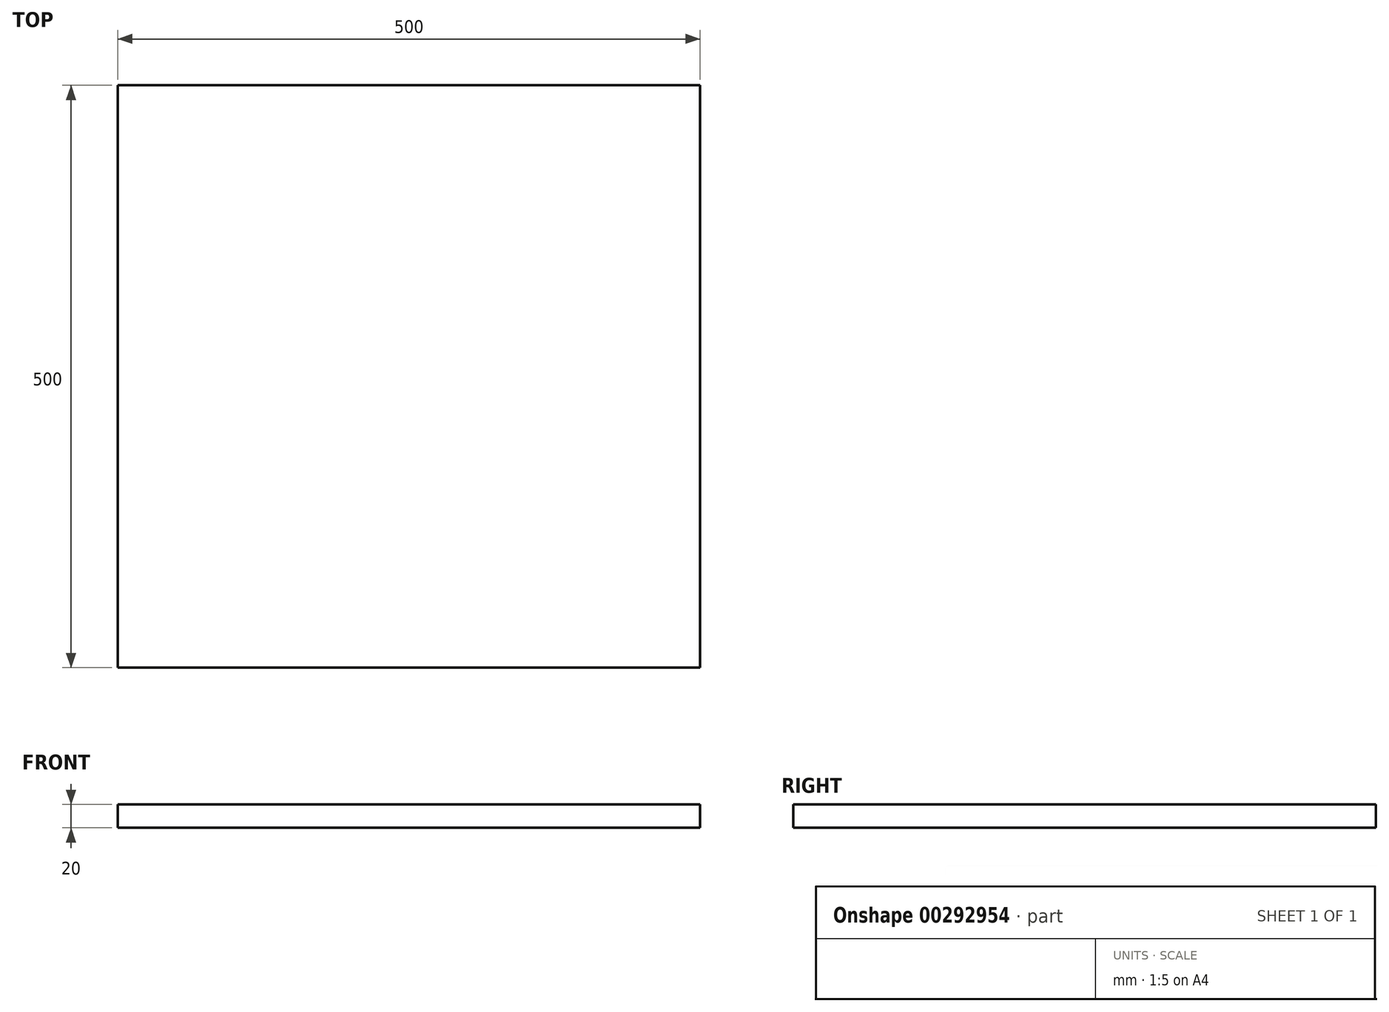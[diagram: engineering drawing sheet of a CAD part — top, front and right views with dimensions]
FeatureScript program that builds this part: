
annotation { "Feature Type Name" : "Feature", "Feature Type Description" : "" }
export const myFeature = defineFeature(function(context is Context, id is Id, definition is map)
    precondition{}
    {
        {
            var Q0;
            Q0=qCreatedBy(makeId("Top.planeOp"),FACE);
            var sketch = newSketch(context, id + "F0", { "sketchPlane" : qUnion([Q0])});
            skLineSegment(sketch, "E0.bottom", {"start": v(250, 250) * mm, "end": v(-250, 250) * mm});
            skLineSegment(sketch, "E0.top", {"start": v(250, -250) * mm, "end": v(-250, -250) * mm});
            skLineSegment(sketch, "E0.left", {"start": v(250, 250) * mm, "end": v(250, -250) * mm});
            skLineSegment(sketch, "E0.right", {"start": v(-250, 250) * mm, "end": v(-250, -250) * mm});
            skPoint(sketch, "E0.middle", {"position": v(0, 0) * mm});
            skSolve(sketch);
        }
        {
            var Q0;
            Q0=makeQuery(id+"F0.imprint","IMPRINT",FACE,{"disambiguationData":[TD([[makeQuery(id+"F0.imprint","IMPRINT",EDGE,{"derivedFrom":sQuery(id+"F0.wireOp",EDGE,"E0.bottom")}),1.0]])]});
            var sketch = newSketch(context, id + "F1", { "sketchPlane" : qUnion([Q0])});
            skLineSegment(sketch, "E1.bottom", {"start": v(-250, 250) * mm, "end": v(250, 250) * mm});
            skLineSegment(sketch, "E1.top", {"start": v(-250, -250) * mm, "end": v(250, -250) * mm});
            skLineSegment(sketch, "E1.left", {"start": v(-250, 250) * mm, "end": v(-250, -250) * mm});
            skLineSegment(sketch, "E1.right", {"start": v(250, 250) * mm, "end": v(250, -250) * mm});
            skPoint(sketch, "E1.middle", {"position": v(0, 0) * mm});
            skSolve(sketch);
        }
        {
            var Q0;
            Q0 = qSketchRegion(id + "F1", true);
            extrude(context, id + "F2", {"entities" : qUnion([Q0]), "depth" : 20 * mm});
        }
    });
